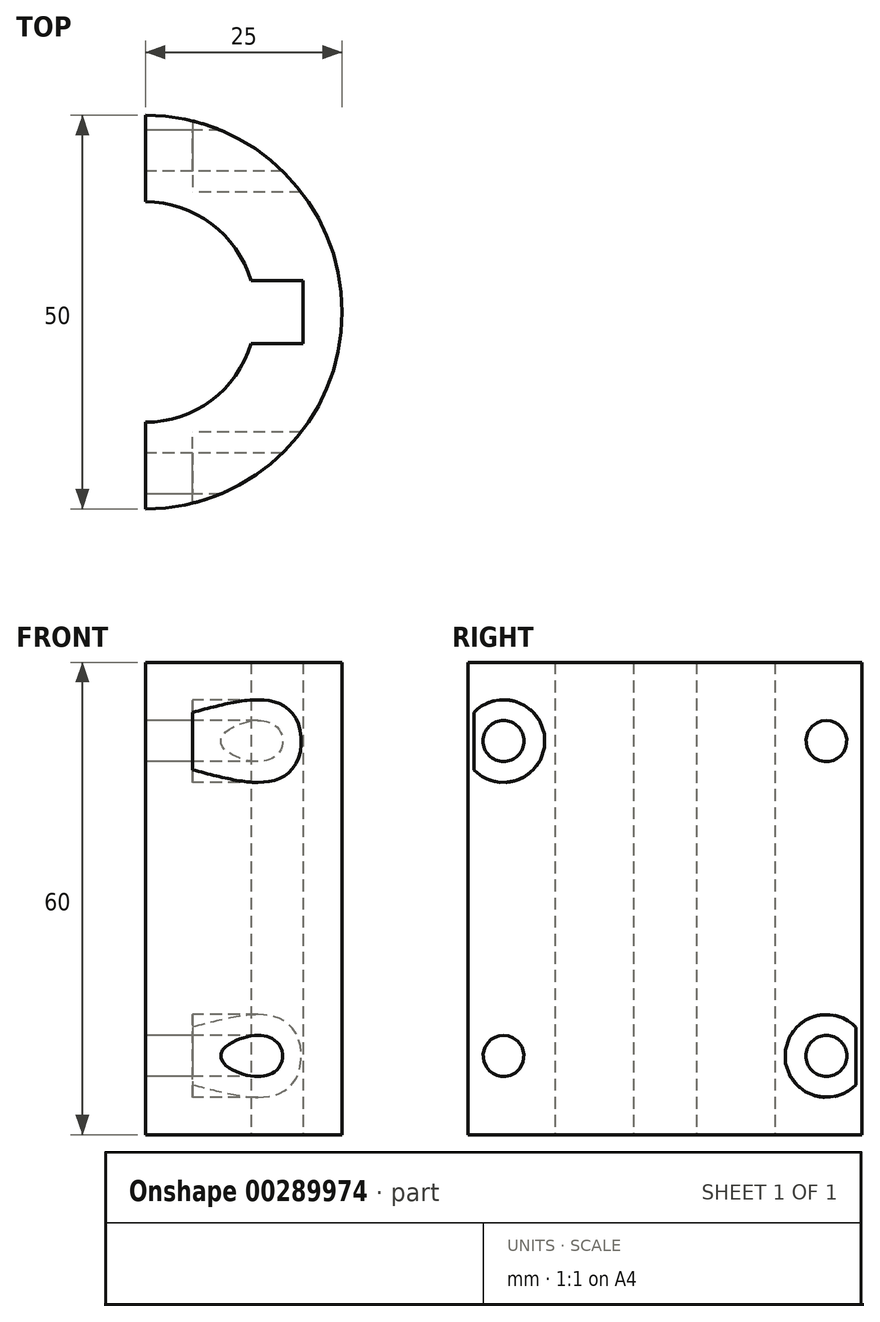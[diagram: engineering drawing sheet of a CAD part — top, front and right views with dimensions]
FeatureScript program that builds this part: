
annotation { "Feature Type Name" : "Feature", "Feature Type Description" : "" }
export const myFeature = defineFeature(function(context is Context, id is Id, definition is map)
    precondition{}
    {
        {
            var Q0;
            Q0=qCreatedBy(makeId("Top.planeOp"),FACE);
            var sketch = newSketch(context, id + "F0", { "sketchPlane" : qUnion([Q0])});
            skArc(sketch, "E0", {"start": v(0, -25) * mm, "mid": v(25, 0) * mm, "end": v(0, 25) * mm});
            skArc(sketch, "E1", {"start": v(0, -14) * mm, "mid": v(14, 0) * mm, "end": v(0, 14) * mm});
            skLineSegment(sketch, "E2", {"start": v(0, 25) * mm, "end": v(0, 14) * mm});
            skLineSegment(sketch, "E3", {"start": v(0, -14) * mm, "end": v(0, -25) * mm});
            skSolve(sketch);
        }
        {
            var Q0;
            Q0=qSketchRegion(id+"F0",true);
            extrude(context, id + "F1", {"entities" : qUnion([Q0]), "depth" : 60 * mm});
        }
        {
            var Q0;
            Q0=qCreatedBy(makeId("Right.planeOp"),FACE);
            var sketch = newSketch(context, id + "F2", { "sketchPlane" : qUnion([Q0])});
            skCircle(sketch, "E4", {"center": v(-20.5, 10) * mm, "radius": 2.6 * mm});
            skCircle(sketch, "E5", {"center": v(-20.5, 50) * mm, "radius": 2.6 * mm});
            skCircle(sketch, "E6", {"center": v(20.5, 50) * mm, "radius": 2.6 * mm});
            skCircle(sketch, "E7", {"center": v(20.5, 10) * mm, "radius": 2.6 * mm});
            skSolve(sketch);
        }
        {
            var Q0;
            Q0=qSketchRegion(id+"F2",true);
            extrude(context, id + "F3", {"entities" : qUnion([Q0]), "operationType" : NewBodyOperationType.REMOVE, "endBound" : BoundingType.THROUGH_ALL, "depth" : 25 * mm});
        }
        {
            var Q0;
            Q0=makeQuery(id+"F1.opExtrude","SWEPT_FACE",FACE,{"disambiguationData":[OSD([sQuery(id+"F0.wireOp",EDGE,"E3")])]});
            cPlane(context, id + "F4", {"entities" : qUnion([Q0]), "cplaneType" : CPlaneType.OFFSET, "offset" : 6 * mm, "oppositeDirection" : true, "width" : 150 * mm, "height" : 150 * mm});
        }
        {
            var Q0;
            Q0=qCreatedBy(id+"F4.planeOp",FACE);
            var sketch = newSketch(context, id + "F5", { "sketchPlane" : qUnion([Q0])});
            skCircle(sketch, "E8", {"center": v(20.5, 50) * mm, "radius": 5.25 * mm});
            skLineSegment(sketch, "E9", {"start": v(20.5, 50) * mm, "end": v(-20.5, 50) * mm});
            skCircle(sketch, "E10", {"center": v(-20.5, 10) * mm, "radius": 5.25 * mm});
            skLineSegment(sketch, "E11", {"start": v(-20.5, 50) * mm, "end": v(-20.5, 10) * mm});
            skSolve(sketch);
        }
        {
            var Q0;
            Q0=qSketchRegion(id+"F5",true);
            extrude(context, id + "F6", {"entities" : qUnion([Q0]), "operationType" : NewBodyOperationType.REMOVE, "oppositeDirection" : true, "depth" : 25 * mm});
        }
        {
            var Q0;
            Q0=qCreatedBy(makeId("Top.planeOp"),FACE);
            var sketch = newSketch(context, id + "F7", { "sketchPlane" : qUnion([Q0])});
            skLineSegment(sketch, "E12.bottom", {"start": v(20, 4) * mm, "end": v(12, 4) * mm});
            skLineSegment(sketch, "E12.top", {"start": v(20, -4) * mm, "end": v(12, -4) * mm});
            skLineSegment(sketch, "E12.left", {"start": v(20, 4) * mm, "end": v(20, -4) * mm});
            skLineSegment(sketch, "E12.right", {"start": v(12, 4) * mm, "end": v(12, -4) * mm});
            skPoint(sketch, "E12.middle", {"position": v(16, 0) * mm});
            skSolve(sketch);
        }
        {
            var Q0;
            Q0=qSketchRegion(id+"F7",true);
            extrude(context, id + "F8", {"entities" : qUnion([Q0]), "operationType" : NewBodyOperationType.REMOVE, "endBound" : BoundingType.THROUGH_ALL, "depth" : 25 * mm});
        }
    });
